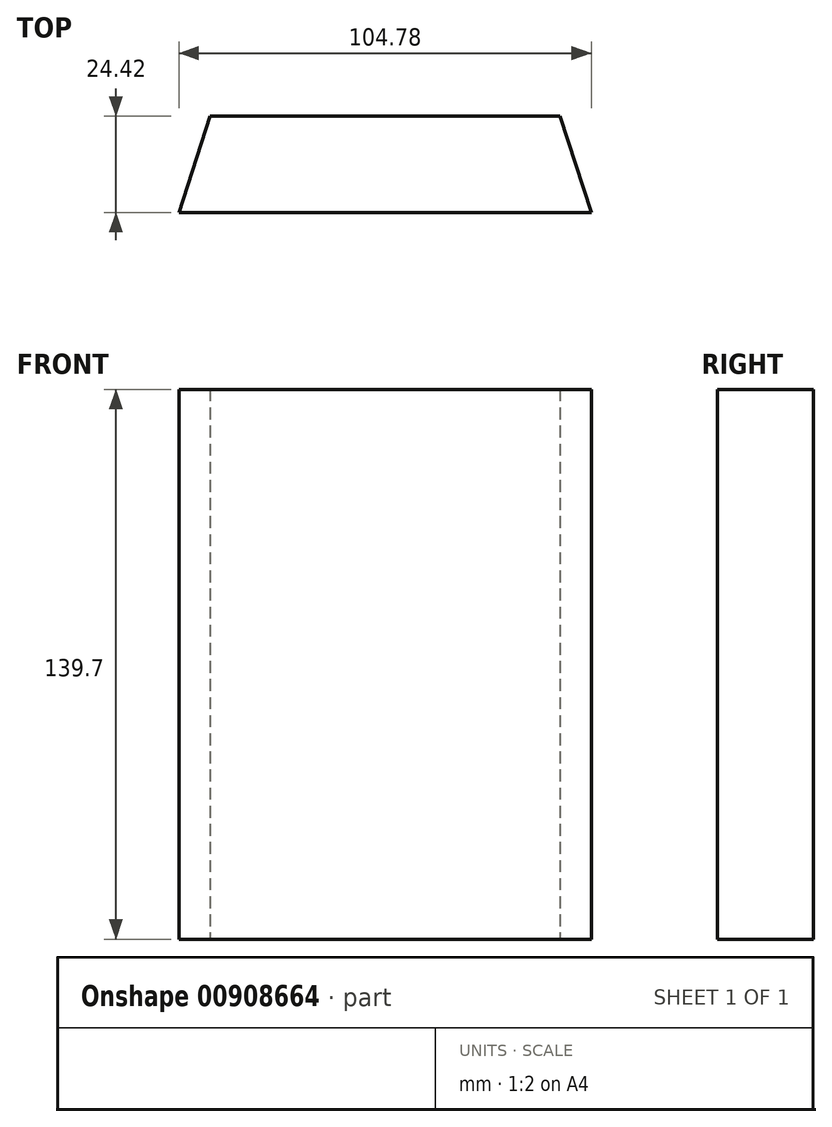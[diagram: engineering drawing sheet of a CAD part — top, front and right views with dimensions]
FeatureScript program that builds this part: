
annotation { "Feature Type Name" : "Feature", "Feature Type Description" : "" }
export const myFeature = defineFeature(function(context is Context, id is Id, definition is map)
    precondition{}
    {
        {
            var Q0;
            Q0=qCreatedBy(makeId("Top.planeOp"),FACE);
            var sketch = newSketch(context, id + "F0", { "sketchPlane" : qUnion([Q0])});
            skLineSegment(sketch, "E0", {"start": v(-52.45, -12.21) * mm, "end": v(52.33, -12.21) * mm});
            skLineSegment(sketch, "E1", {"start": v(52.33, -12.21) * mm, "end": v(44.39, 12.21) * mm});
            skLineSegment(sketch, "E2", {"start": v(44.39, 12.21) * mm, "end": v(-44.51, 12.21) * mm});
            skLineSegment(sketch, "E3", {"start": v(-44.51, 12.21) * mm, "end": v(-52.45, -12.21) * mm});
            skLineSegment(sketch, "E4", {"start": v(-86.46, 0) * mm, "end": v(0, 0) * mm, "construction": true});
            skLineSegment(sketch, "E5", {"start": v(0, 0) * mm, "end": v(0, -66.99) * mm, "construction": true});
            skSolve(sketch);
        }
        {
            var Q0;
            Q0=makeQuery(id+"F0.imprint","IMPRINT",FACE,{"disambiguationData":[TD([[makeQuery(id+"F0.imprint","IMPRINT",EDGE,{"derivedFrom":sQuery(id+"F0.wireOp",EDGE,"E0")}),1.0]])]});
            extrude(context, id + "F1", {"entities" : qUnion([Q0]), "depth" : 139.7 * mm, "offsetDistance" : 25.4 * mm});
        }
    });
